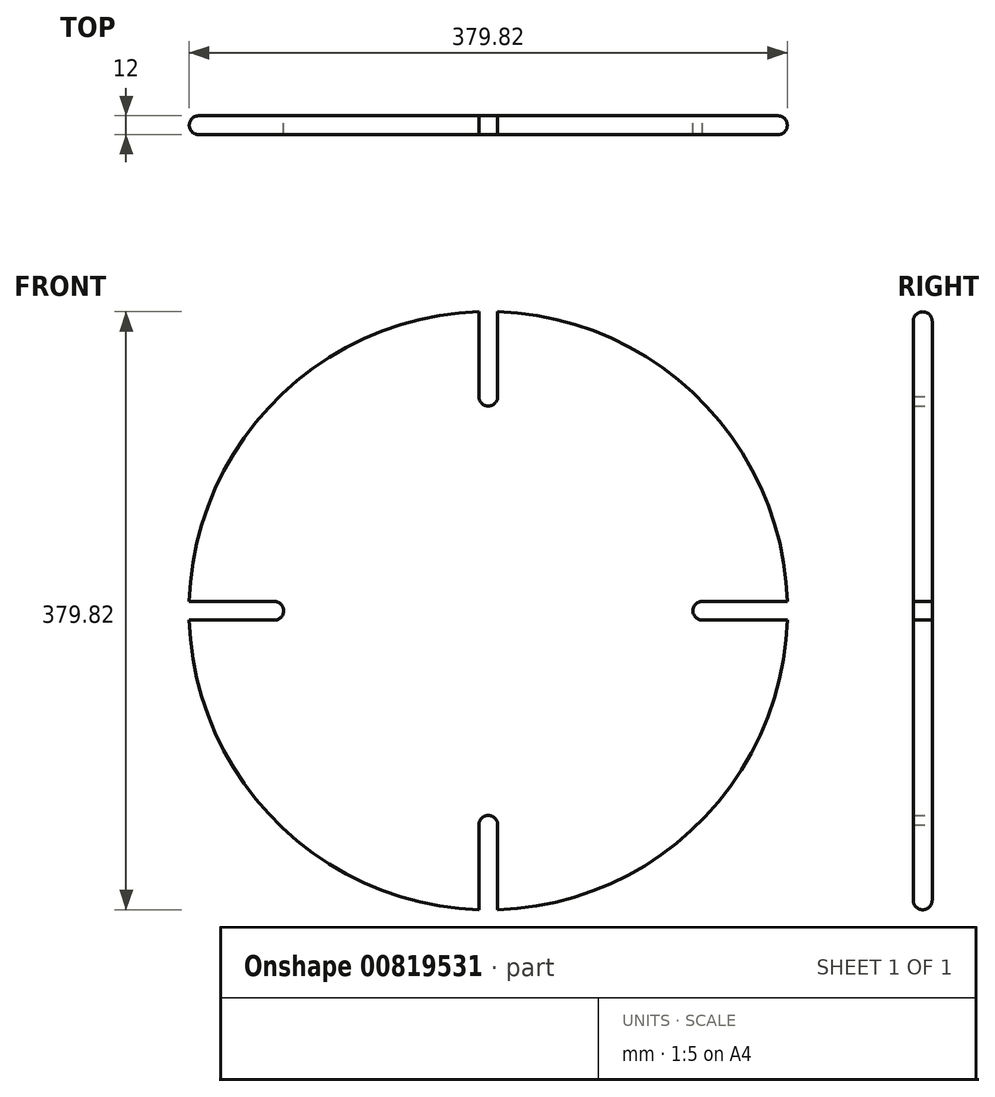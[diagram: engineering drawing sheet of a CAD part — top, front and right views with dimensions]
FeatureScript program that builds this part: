
annotation { "Feature Type Name" : "Feature", "Feature Type Description" : "" }
export const myFeature = defineFeature(function(context is Context, id is Id, definition is map)
    precondition{}
    {
        {
            var Q0;
            Q0=qCreatedBy(makeId("Front.planeOp"),FACE);
            var sketch = newSketch(context, id + "F0", { "sketchPlane" : qUnion([Q0])});
            skArc(sketch, "E0", {"start": v(-6, 189.9) * mm, "mid": v(-134.35, 134.35) * mm, "end": v(-189.9, 6) * mm});
            skArc(sketch, "E1", {"start": v(-6, 136.13) * mm, "mid": v(0, 130) * mm, "end": v(6, 136.13) * mm});
            skArc(sketch, "E2", {"start": v(135.87, 6) * mm, "mid": v(130, -0.13) * mm, "end": v(136.13, -6) * mm});
            skArc(sketch, "E3", {"start": v(6, -136.13) * mm, "mid": v(0, -130) * mm, "end": v(-6, -136.13) * mm});
            skArc(sketch, "E4", {"start": v(-136, -6) * mm, "mid": v(-130, 0) * mm, "end": v(-136, 6) * mm});
            skLineSegment(sketch, "E5", {"start": v(6, 135.87) * mm, "end": v(6, 189.9) * mm});
            skLineSegment(sketch, "E6", {"start": v(-6, 135.87) * mm, "end": v(-6, 189.9) * mm});
            skLineSegment(sketch, "E7", {"start": v(135.87, 6) * mm, "end": v(189.9, 6) * mm});
            skLineSegment(sketch, "E8", {"start": v(135.87, -6) * mm, "end": v(189.9, -6) * mm});
            skArc(sketch, "E9.trimOffspring", {"start": v(189.9, 6) * mm, "mid": v(134.35, 134.35) * mm, "end": v(6, 189.9) * mm});
            skLineSegment(sketch, "E10", {"start": v(-6, -135.87) * mm, "end": v(-6, -189.9) * mm});
            skLineSegment(sketch, "E11", {"start": v(6, -135.87) * mm, "end": v(6, -189.9) * mm});
            skArc(sketch, "E12.trimOffspring", {"start": v(6, -189.9) * mm, "mid": v(134.35, -134.35) * mm, "end": v(189.9, -6) * mm});
            skLineSegment(sketch, "E13", {"start": v(-136, 6) * mm, "end": v(-189.9, 6) * mm});
            skLineSegment(sketch, "E14", {"start": v(-136, -6) * mm, "end": v(-189.9, -6) * mm});
            skArc(sketch, "E15.trimOffspring", {"start": v(-189.9, -6) * mm, "mid": v(-134.35, -134.35) * mm, "end": v(-6, -189.9) * mm});
            skSolve(sketch);
        }
        {
            var Q0;
            {var subQ12=sQuery(id+"F0.wireOp",EDGE,"E0");Q0=makeQuery(id+"F0.imprint","IMPRINT",FACE,{"disambiguationData":[TD([[makeQuery(id+"F0.imprint","IMPRINT",EDGE,{"derivedFrom":subQ12}),1.0]])]});}
            extrude(context, id + "F1", {"entities" : qUnion([Q0]), "depth" : 12 * mm, "offsetDistance" : 25 * mm});
        }
        {
            var Q0;
            Q0=makeQuery(id+"F1.opExtrude","CAP_EDGE",EDGE,{"disambiguationData":[OSD([sQuery(id+"F0.wireOp",EDGE,"E12.trimOffspring")])],"isStart":false});
            var Q1;
            Q1=makeQuery(id+"F1.opExtrude","CAP_EDGE",EDGE,{"disambiguationData":[OSD([sQuery(id+"F0.wireOp",EDGE,"E12.trimOffspring")])],"isStart":true});
            var Q2;
            Q2=makeQuery(id+"F1.opExtrude","CAP_EDGE",EDGE,{"disambiguationData":[OSD([sQuery(id+"F0.wireOp",EDGE,"E15.trimOffspring")])],"isStart":false});
            var Q3;
            Q3=makeQuery(id+"F1.opExtrude","CAP_EDGE",EDGE,{"disambiguationData":[OSD([sQuery(id+"F0.wireOp",EDGE,"E15.trimOffspring")])],"isStart":true});
            var Q4;
            Q4=makeQuery(id+"F1.opExtrude","CAP_EDGE",EDGE,{"disambiguationData":[OSD([sQuery(id+"F0.wireOp",EDGE,"E9.trimOffspring")])],"isStart":false});
            var Q5;
            Q5=makeQuery(id+"F1.opExtrude","CAP_EDGE",EDGE,{"disambiguationData":[OSD([sQuery(id+"F0.wireOp",EDGE,"E9.trimOffspring")])],"isStart":true});
            var Q6;
            Q6=makeQuery(id+"F1.opExtrude","CAP_EDGE",EDGE,{"disambiguationData":[OSD([sQuery(id+"F0.wireOp",EDGE,"E0")])],"isStart":true});
            var Q7;
            Q7=makeQuery(id+"F1.opExtrude","CAP_EDGE",EDGE,{"disambiguationData":[OSD([sQuery(id+"F0.wireOp",EDGE,"E0")])],"isStart":false});
            fillet(context, id + "F2", {"entities" : qUnion([Q0, Q1, Q2, Q3, Q4, Q5, Q6, Q7]), "radius" : 6 * mm, "tangentPropagation" : true, "allowEdgeOverflow" : false});
        }
    });
